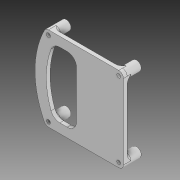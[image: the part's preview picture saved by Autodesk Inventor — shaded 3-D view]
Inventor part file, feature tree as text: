
AUTODESK INVENTOR PART (.ipt)
format: ipt  version: 2021 (Build 250183000, 183)  size: 200,704 bytes
history: native  units: in
note: dims shown in document units (in); Inventor stores cm internally (conversion verified against a paired STEP export)
features: extrude x2, fillet x2, sketch x2, reference x2, other x2
ambient origin geometry x8: Origin, YZ Plane, XZ Plane, XY Plane, X Axis, Y Axis, Z Axis, Center Point
bodies: Solid1 (feature_tree)
feature tree (10):
  extrude  "Extrusion1"  Depth=0.3937in
  extrude  "Extrusion2"  Depth=1.9685in
  fillet  "Fillet1"  Radius=0.4724in
  fillet  "Fillet2"  Radius=0.1575in
  sketch  "Sketch1"  dims[d0=0.5906in d1=0.0in d2=0.3937in]
  reference  "Reference1"
  sketch  "Sketch2"  dims[d3=0.3937in d4=1.9685in d5=0.4724in d6=0.1575in d7=0.0in d8=0.3937in d9=0.1575in]
  reference  "Reference2"
  other  "Impedance_Analyzer_V2.iam"
  other  "Bottom Case:1"
